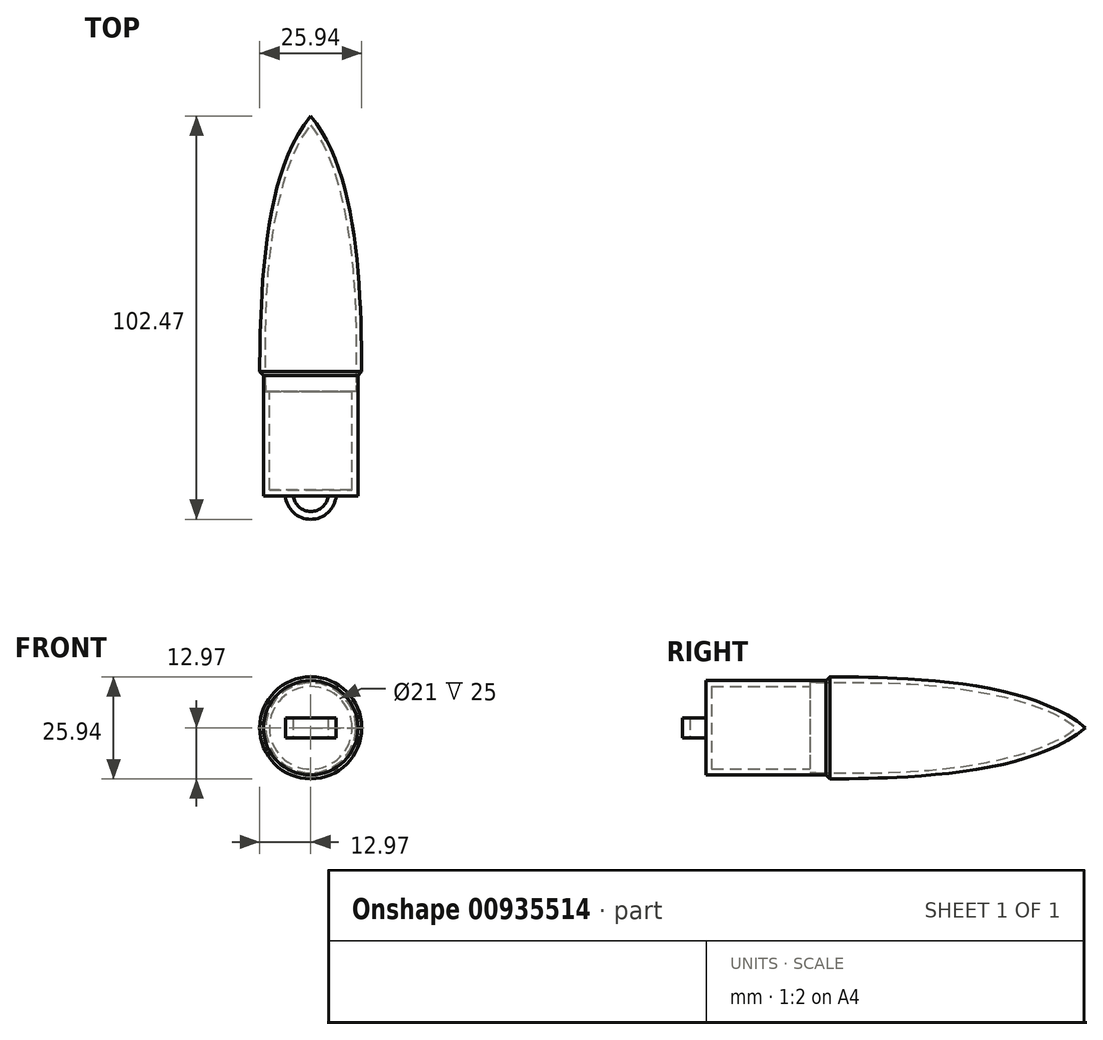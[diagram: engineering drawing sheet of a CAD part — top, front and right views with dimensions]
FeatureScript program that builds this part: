
annotation { "Feature Type Name" : "Feature", "Feature Type Description" : "" }
export const myFeature = defineFeature(function(context is Context, id is Id, definition is map)
    precondition{}
    {
        {
            var Q0;
            Q0=qCreatedBy(makeId("Top.planeOp"),FACE);
            var sketch = newSketch(context, id + "F0", { "sketchPlane" : qUnion([Q0])});
            skLineSegment(sketch, "E0", {"start": v(0, 70) * mm, "end": v(0, 0) * mm});
            skLineSegment(sketch, "E1", {"start": v(0, 0) * mm, "end": v(13, 0) * mm});
            skFitSpline(sketch, "E2", {"points": [v(0, 70) * mm, v(13, 0) * mm], "startDerivative": vector(37.08, -44.95) * mm, "endDerivative": vector(0.23, -75.14) * mm});
            skFitSpline(sketch, "E3.0", {"points": [v(-1.16, 69.05) * mm, v(0.31, 67.27) * mm, v(2.92, 63.23) * mm, v(5.95, 55.95) * mm, v(8.17, 47.68) * mm, v(10.23, 35.65) * mm, v(11.38, 19.36) * mm, v(11.48, 6.25) * mm, v(11.5, 0) * mm]});
            skLineSegment(sketch, "E4.bottom", {"start": v(10.5, 1.5) * mm, "end": v(12, 1.5) * mm});
            skLineSegment(sketch, "E4.top", {"start": v(10.5, -26.5) * mm, "end": v(12, -26.5) * mm});
            skLineSegment(sketch, "E4.left", {"start": v(10.5, 1.5) * mm, "end": v(10.5, -26.5) * mm});
            skLineSegment(sketch, "E4.right", {"start": v(12, 1.5) * mm, "end": v(12, -26.5) * mm});
            skLineSegment(sketch, "E5.bottom", {"start": v(10.5, -26.5) * mm, "end": v(0, -26.5) * mm});
            skLineSegment(sketch, "E5.top", {"start": v(10.5, -25) * mm, "end": v(0, -25) * mm});
            skLineSegment(sketch, "E5.left", {"start": v(10.5, -26.5) * mm, "end": v(10.5, -25) * mm});
            skLineSegment(sketch, "E5.right", {"start": v(0, -26.5) * mm, "end": v(0, -25) * mm});
            skFitSpline(sketch, "E6", {"points": [v(10.5, -26.5) * mm, v(0, -33.95) * mm], "startDerivative": vector(-4.15, -6.49) * mm, "endDerivative": vector(-19.26, -0.88) * mm});
            skLineSegment(sketch, "E7", {"start": v(0, -26.5) * mm, "end": v(0, -33.95) * mm});
            skSolve(sketch);
        }
        {
            var Q0;
            {var subQ0=sQuery(id+"F0.wireOp",EDGE,"E2");Q0=makeQuery(id+"F0.imprint","IMPRINT",FACE,{"disambiguationData":[TD([[makeQuery(id+"F0.imprint","IMPRINT",EDGE,{"derivedFrom":subQ0}),-1.0]])]});}
            var Q1;
            {var subQ0=sQuery(id+"F0.wireOp",EDGE,"E4.top");Q1=makeQuery(id+"F0.imprint","IMPRINT",FACE,{"disambiguationData":[TD([[makeQuery(id+"F0.imprint","IMPRINT",EDGE,{"derivedFrom":subQ0}),1.0]])]});}
            var Q2;
            {var subQ0=sQuery(id+"F0.wireOp",EDGE,"E3.0");var subQ1=sQuery(id+"F0.wireOp",EDGE,"E1");var subQ2=makeQuery(id+"F0.imprint","INTERSECT",VERTEX,{"derivedFrom":[subQ1,subQ0]});Q2=makeQuery(id+"F0.imprint","IMPRINT",FACE,{"disambiguationData":[TD([[makeQuery(id+"F0.imprint","IMPRINT",EDGE,{"disambiguationData":[TD([[subQ2,-1.0]])],"derivedFrom":subQ1}),1.0]])]});}
            var Q3;
            Q3=makeQuery(id+"F0.imprint","IMPRINT",FACE,{"disambiguationData":[TD([[makeQuery(id+"F0.imprint","IMPRINT",EDGE,{"derivedFrom":sQuery(id+"F0.wireOp",EDGE,"E5.bottom")}),-1.0]])]});
            var Q4;
            Q4=sQuery(id+"F0.wireOp",EDGE,"E0");
            revolve(context, id + "F1", {"surfaceOperationType" : NewSurfaceOperationType.NEW, "entities" : qUnion([Q0, Q1, Q2, Q3]), "axis" : qUnion([Q4]), "revolveType" : RevolveType.FULL});
        }
        {
            var Q0;
            Q0=qCreatedBy(makeId("Top.planeOp"),FACE);
            var sketch = newSketch(context, id + "F2", { "sketchPlane" : qUnion([Q0])});
            skArc(sketch, "E8", {"start": v(-6.44, -26.5) * mm, "mid": v(0, -32.47) * mm, "end": v(6.45, -26.5) * mm});
            skLineSegment(sketch, "E9", {"start": v(-6.44, -26.5) * mm, "end": v(6.45, -26.5) * mm});
            skArc(sketch, "E10.0", {"start": v(-4.45, -26.35) * mm, "mid": v(0, -30.47) * mm, "end": v(4.46, -26.35) * mm});
            skSolve(sketch);
        }
        {
            var Q0;
            {var subQ0=sQuery(id+"F2.wireOp",EDGE,"E8");Q0=makeQuery(id+"F2.imprint","IMPRINT",FACE,{"disambiguationData":[TD([[makeQuery(id+"F2.imprint","IMPRINT",EDGE,{"derivedFrom":subQ0}),1.0]])]});}
            extrude(context, id + "F3", {"entities" : qUnion([Q0]), "operationType" : NewBodyOperationType.ADD, "endBound" : BoundingType.SYMMETRIC, "depth" : 5 * mm, "offsetDistance" : 25 * mm});
        }
        {
            var Q0;
            Q0=makeQuery(id+"F1.opRevolve","SWEPT_FACE",FACE,{"disambiguationData":[OSD([sQuery(id+"F0.wireOp",EDGE,"E2")])]});
            chamfer(context, id + "F4", {"entities" : qUnion([Q0]), "width" : 5 * mm, "tangentPropagation" : true});
        }
    });
